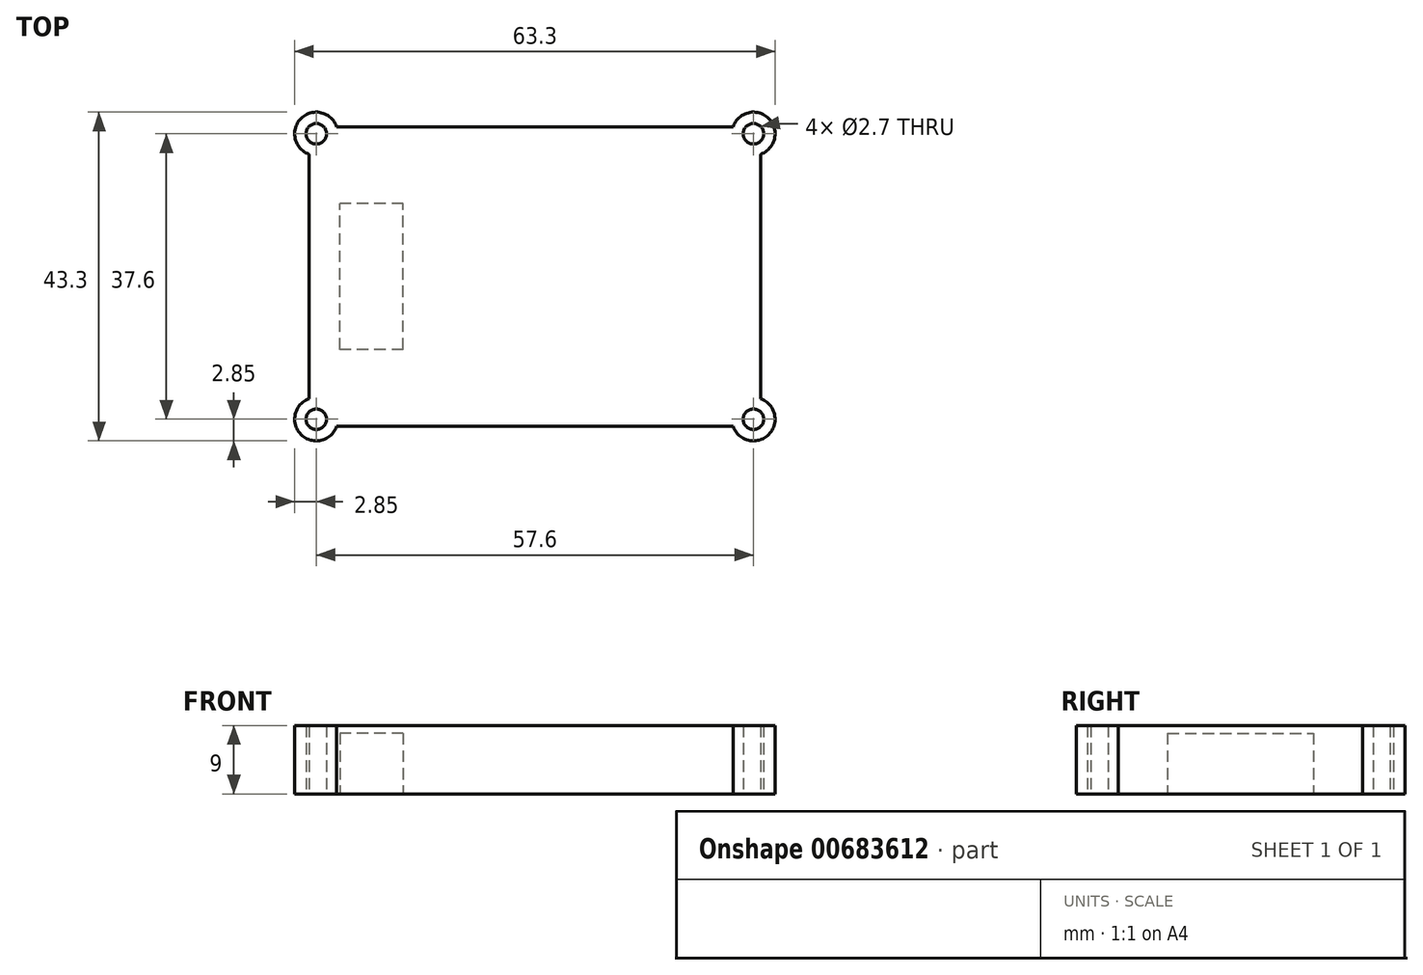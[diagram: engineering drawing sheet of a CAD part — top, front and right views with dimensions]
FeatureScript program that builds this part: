
annotation { "Feature Type Name" : "Feature", "Feature Type Description" : "" }
export const myFeature = defineFeature(function(context is Context, id is Id, definition is map)
    precondition{}
    {
        {
            var Q0;
            Q0=qCreatedBy(makeId("Top.planeOp"),FACE);
            var sketch = newSketch(context, id + "F0", { "sketchPlane" : qUnion([Q0])});
            skLineSegment(sketch, "E0.bottom", {"start": v(-26.1, 19.73) * mm, "end": v(26.1, 19.73) * mm});
            skLineSegment(sketch, "E0.top", {"start": v(-26.1, -19.73) * mm, "end": v(26.1, -19.73) * mm});
            skPoint(sketch, "E0.middle", {"position": v(0, 0) * mm});
            skCircle(sketch, "E1", {"center": v(-28.8, 18.8) * mm, "radius": 1.35 * mm});
            skCircle(sketch, "E2.MirrorC", {"center": v(28.8, 18.8) * mm, "radius": 1.35 * mm});
            skLineSegment(sketch, "E3.MirrorCS", {"start": v(26.1, 19.73) * mm, "end": v(-26.1, 19.73) * mm});
            skCircle(sketch, "E4.MirrorC", {"center": v(-28.8, -18.8) * mm, "radius": 1.35 * mm});
            skCircle(sketch, "E5.MirrorC", {"center": v(28.8, -18.8) * mm, "radius": 1.35 * mm});
            skArc(sketch, "E6", {"start": v(-26.1, 19.73) * mm, "mid": v(-30.82, 20.82) * mm, "end": v(-29.72, 16.1) * mm});
            skLineSegment(sketch, "E7.trimOffspring", {"start": v(-29.72, 16.1) * mm, "end": v(-29.73, -16.1) * mm});
            skPoint(sketch, "E8.orphan", {"position": v(-29.73, 19.73) * mm});
            skPoint(sketch, "E9.orphan", {"position": v(-29.72, 19.73) * mm});
            skArc(sketch, "E10.MirrorCS", {"start": v(26.1, 19.73) * mm, "mid": v(30.82, 20.82) * mm, "end": v(29.72, 16.1) * mm});
            skArc(sketch, "E11.MirrorCS", {"start": v(-26.1, -19.73) * mm, "mid": v(-30.82, -20.82) * mm, "end": v(-29.72, -16.1) * mm});
            skArc(sketch, "E12.MirrorCS", {"start": v(26.1, -19.73) * mm, "mid": v(30.82, -20.82) * mm, "end": v(29.72, -16.1) * mm});
            skLineSegment(sketch, "E13.trimOffspring", {"start": v(29.73, 16.1) * mm, "end": v(29.72, -16.1) * mm});
            skPoint(sketch, "E14.orphan", {"position": v(29.72, 19.73) * mm});
            skPoint(sketch, "E15.orphan", {"position": v(29.73, 19.73) * mm});
            skPoint(sketch, "E16.trimOffspring.end.orphan", {"position": v(29.72, -19.73) * mm});
            skPoint(sketch, "E17.orphan", {"position": v(-29.72, -19.73) * mm});
            skSolve(sketch);
        }
        {
            var Q0;
            Q0 = qSketchRegion(id + "F0", true);
            extrude(context, id + "F1", {"entities" : qUnion([Q0]), "depth" : 9 * mm, "offsetDistance" : 25 * mm});
        }
        {
            var Q0;
            Q0=makeQuery(id+"F1.opExtrude","CAP_FACE",FACE,{"disambiguationData":[OSD([sQuery(id+"F0.wireOp",EDGE,"E0.top"),sQuery(id+"F0.wireOp",EDGE,"E3.MirrorCS"),sQuery(id+"F0.wireOp",EDGE,"E1"),sQuery(id+"F0.wireOp",EDGE,"E2.MirrorC"),sQuery(id+"F0.wireOp",EDGE,"E4.MirrorC"),sQuery(id+"F0.wireOp",EDGE,"E5.MirrorC"),sQuery(id+"F0.wireOp",EDGE,"E6"),sQuery(id+"F0.wireOp",EDGE,"E7.trimOffspring"),sQuery(id+"F0.wireOp",EDGE,"E10.MirrorCS"),sQuery(id+"F0.wireOp",EDGE,"E11.MirrorCS"),sQuery(id+"F0.wireOp",EDGE,"E12.MirrorCS"),sQuery(id+"F0.wireOp",EDGE,"E13.trimOffspring")])],"isStart":true});
            var sketch = newSketch(context, id + "F2", { "sketchPlane" : qUnion([Q0])});
            skLineSegment(sketch, "E18.bottom", {"start": v(-17.35, 9.6) * mm, "end": v(-25.7, 9.6) * mm});
            skLineSegment(sketch, "E18.top", {"start": v(-17.35, -9.6) * mm, "end": v(-25.7, -9.6) * mm});
            skLineSegment(sketch, "E18.left", {"start": v(-17.35, 9.6) * mm, "end": v(-17.35, -9.6) * mm});
            skLineSegment(sketch, "E18.right", {"start": v(-25.7, 9.6) * mm, "end": v(-25.7, -9.6) * mm});
            skPoint(sketch, "E18.middle", {"position": v(-21.52, 0) * mm});
            skSolve(sketch);
        }
        {
            var Q0;
            Q0 = qSketchRegion(id + "F2", true);
            extrude(context, id + "F3", {"entities" : qUnion([Q0]), "operationType" : NewBodyOperationType.REMOVE, "oppositeDirection" : true, "depth" : 8 * mm, "offsetDistance" : 25 * mm});
        }
    });
